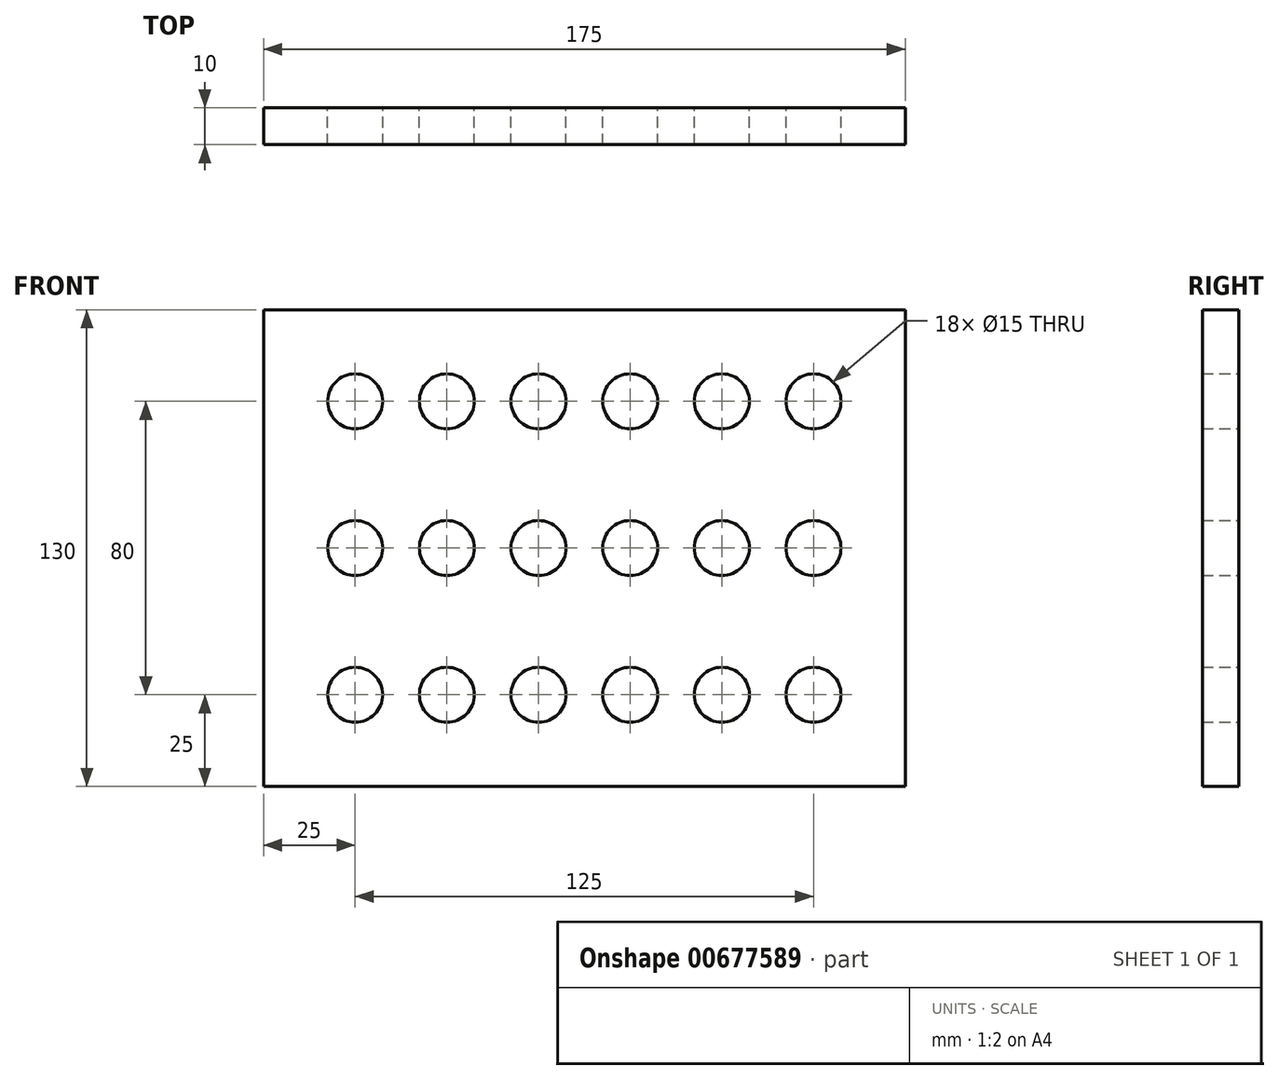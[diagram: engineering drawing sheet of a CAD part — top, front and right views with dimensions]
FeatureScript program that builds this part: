
annotation { "Feature Type Name" : "Feature", "Feature Type Description" : "" }
export const myFeature = defineFeature(function(context is Context, id is Id, definition is map)
    precondition{}
    {
        {
            var Q0;
            Q0=qCreatedBy(makeId("Front.planeOp"),FACE);
            var sketch = newSketch(context, id + "F0", { "sketchPlane" : qUnion([Q0])});
            skLineSegment(sketch, "E0.bottom", {"start": v(-87.5, 65) * mm, "end": v(87.5, 65) * mm});
            skLineSegment(sketch, "E0.top", {"start": v(-87.5, -65) * mm, "end": v(87.5, -65) * mm});
            skLineSegment(sketch, "E0.left", {"start": v(-87.5, 65) * mm, "end": v(-87.5, -65) * mm});
            skLineSegment(sketch, "E0.right", {"start": v(87.5, 65) * mm, "end": v(87.5, -65) * mm});
            skPoint(sketch, "E0.middle", {"position": v(0, 0) * mm});
            skCircle(sketch, "E1", {"center": v(-62.5, 40) * mm, "radius": 7.5 * mm});
            skCircle(sketch, "E2.1.0.0", {"center": v(-37.5, 40) * mm, "radius": 7.5 * mm});
            skCircle(sketch, "E2.2.0.0", {"center": v(-12.5, 40) * mm, "radius": 7.5 * mm});
            skCircle(sketch, "E2.3.0.0", {"center": v(12.5, 40) * mm, "radius": 7.5 * mm});
            skCircle(sketch, "E2.4.0.0", {"center": v(37.5, 40) * mm, "radius": 7.5 * mm});
            skCircle(sketch, "E2.5.0.0", {"center": v(62.5, 40) * mm, "radius": 7.5 * mm});
            skLineSegment(sketch, "E2.direction1", {"start": v(-62.5, 40) * mm, "end": v(-37.5, 40) * mm, "construction": true});
            skCircle(sketch, "E3.0.1.0", {"center": v(-62.5, 0) * mm, "radius": 7.5 * mm});
            skCircle(sketch, "E3.0.2.0", {"center": v(-62.5, -40) * mm, "radius": 7.5 * mm});
            skCircle(sketch, "E3.1.1.0", {"center": v(-37.5, 0) * mm, "radius": 7.5 * mm});
            skCircle(sketch, "E3.1.2.0", {"center": v(-37.5, -40) * mm, "radius": 7.5 * mm});
            skCircle(sketch, "E3.2.1.0", {"center": v(-12.5, 0) * mm, "radius": 7.5 * mm});
            skCircle(sketch, "E3.2.2.0", {"center": v(-12.5, -40) * mm, "radius": 7.5 * mm});
            skLineSegment(sketch, "E3.direction2", {"start": v(-62.5, 40) * mm, "end": v(-62.5, 0) * mm, "construction": true});
            skCircle(sketch, "E4.0.3.1", {"center": v(12.5, 0) * mm, "radius": 7.5 * mm});
            skCircle(sketch, "E4.0.3.2", {"center": v(12.5, -40) * mm, "radius": 7.5 * mm});
            skCircle(sketch, "E4.0.4.1", {"center": v(37.5, 0) * mm, "radius": 7.5 * mm});
            skCircle(sketch, "E4.0.4.2", {"center": v(37.5, -40) * mm, "radius": 7.5 * mm});
            skCircle(sketch, "E4.0.5.1", {"center": v(62.5, 0) * mm, "radius": 7.5 * mm});
            skCircle(sketch, "E4.0.5.2", {"center": v(62.5, -40) * mm, "radius": 7.5 * mm});
            skSolve(sketch);
        }
        {
            var Q0;
            Q0=makeQuery(id+"F0.imprint","IMPRINT",FACE,{"disambiguationData":[TD([[makeQuery(id+"F0.imprint","IMPRINT",EDGE,{"derivedFrom":sQuery(id+"F0.wireOp",EDGE,"E0.bottom")}),-1.0]])]});
            extrude(context, id + "F1", {"entities" : qUnion([Q0]), "depth" : 5 * mm, "offsetDistance" : 25 * mm, "hasSecondDirection" : true, "secondDirectionOppositeDirection" : true, "secondDirectionDepth" : 5 * mm});
        }
    });
